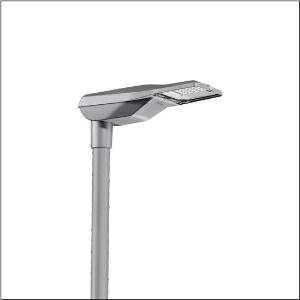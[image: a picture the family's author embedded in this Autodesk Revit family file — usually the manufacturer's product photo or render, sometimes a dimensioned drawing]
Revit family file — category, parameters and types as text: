
# Revit family: streetlight_sl_21_iq_micro___st0_8a_5xe1c61d08cb_7ac8
name_source: partatom
category: Lighting Fixtures
units: mm (PartAtom-declared; Revit-internal decimal feet)

## family parameters
Cut with Voids When Loaded = No
Host = Face
Light Source = No
Part Type = Normal
Room Calculation Point = No
Round Connector Dimension = Use Diameter
Shared = No

## types (1)
- --- (1 x LED, 2570 lm, 19.4 W, 2700K)
    Apparent Load = 19 VA
    CIE Flux Codes = 38 75 97 100 100
    Color Rendering = 70
    Color Temperature = 2700K
    Default Elevation = 1800 mm
    Description = Streetlight SL 21 iQ micro, mast luminaire, primary light control with lens, of PMMA, primary optical cover: cover, of toughened safety glass, transparent, light distribution: ST0.8a, light emission: direct distribution, primary light characteristic: asymmetric, installation type: post-top, side-entry, LED, High Power LED, rated luminous flux: 2.570lm, luminous efficacy: 133lm/W, light colour: 727, colour temperature: 2700K, control: Auto-Match, Temp-Guard, Lumen-Switch, Night-Set, Smart-Wire, Light-Fading, Desk-Remote (wireless, voltage-free reading and setting of iQ features in the workshop via application-optimized NFC function/RFID function), optimised constant luminous flux control (CLO 2.0), presetting dimming linear, mains connection: 220..240V, AC, 50/60Hz, start of lifetime: 19W, end of service life: 20W, reduction: 10W, luminaire housing, of diecast aluminium, powder-coated, Siteco® metallic grey (DB 702S), corrosivity category C5 mid according to DIN EN ISO 12944, please order mast flange separately, inclination adjustable: 0°, 5°, 10°, 15°, sealing non-destructively replaceable, multi-level sealing system, length: 528mm, width: 235mm, height: 110mm, mast flange for spigot size: 42mm (side-entry): 5XC10008XM4, 60/48mm (side-entry/post-top): 5XC10108XM2, 76/60mm (side-entry/post-top): 5XC10108XM1, protection rating (complete): IP66, insulation class (complete): insulation class II (safety insulation), certification: CE, ENEC, ENEC+, VDE, impact resistance: IK09, permissible operating ambient temperature for outdoor applications: -40..+50°C, standard-compliant lighting for roads and squares, packaging unit: 1 piece

Light Distribution: ST0.8a
    Height = 110 mm
    Lamp = 1 x LED
    Lamp Light Flux = 2570 lm
    Lamp Power = 19.4 W
    Lamp count = 1
    Length = 528 mm
    Luminous efficacy = 132 lm/W
    Manufacturer = Siteco
    ModVariant = No
    Model = 5XE1C61D08CB
    Number of Poles = 1
    OnlyDefault = Yes
    Power Factor = 1
    Product Name = Streetlight SL 21 iQ micro | ST0.8a
    Product group = mast luminaire | pylon top
    ProductGroupID = 6100
    Protection Class = Protection class II
    Protection Degree = IP 66
    RLX_Detail_Level = 1
    RLX_Emergency_Light_Flux = 0 lm
    RLX_Emergency_Type = 0
    RLX_Emergency_Type_DB = No
    RlxData = <blob elided: 98849 chars, md5=591a3692>
    Socket = socket
    Standby Power = 0 W
    System Light Flux = 2570 lm
    System Power = 19 W
    Type Comments = factory setting: luminous flux: 100 % | dim-lin: 254 | 387 mA
    Type Image = l_1006881.jpg
    URL = http://relux.com
    VarID = @adj_069645
    Voltage = 0 V
    Weight = 0.00 kg
    Width = 235 mm

## geometry (parser evidence)
native form markers: Blend x4, Sweep x10
no freeform markers — native parametric forms only
